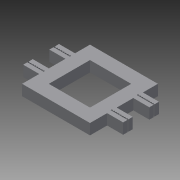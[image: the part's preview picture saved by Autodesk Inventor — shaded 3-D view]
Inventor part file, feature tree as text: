
AUTODESK INVENTOR PART (.ipt)
format: ipt  version: 2014 SP1 (Build 180222100, 222)  size: 249,856 bytes
history: native  units: mm
features: extrude x1, sketch x1
ambient origin geometry x8: Origin, YZ Plane, XZ Plane, XY Plane, X Axis, Y Axis, Z Axis, Center Point
bodies: Solid1 (feature_tree)
feature tree (2):
  extrude  "Extrusion1"  Depth=16.0mm
  sketch  "Sketch1"  dims[d0=63.5mm d5=16.0mm d6=12.5mm d7=12.5mm d8=12.5mm d9=12.5mm d11=15.0mm d12=9.0mm d16=10.0mm d17=0.0mm]
